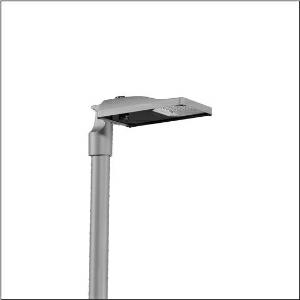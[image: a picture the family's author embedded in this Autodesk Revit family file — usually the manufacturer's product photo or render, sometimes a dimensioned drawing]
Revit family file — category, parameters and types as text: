
# Revit family: streetlight_sl_31_micro___pl52_5xh5h31t08ca_bf49
name_source: partatom
category: Lighting Fixtures
units: mm (PartAtom-declared; Revit-internal decimal feet)

## family parameters
Cut with Voids When Loaded = No
Host = Face
Light Source = No
Part Type = Normal
Room Calculation Point = No
Round Connector Dimension = Use Diameter
Shared = No

## types (1)
- --- (1 x LED, 1420 lm, 10.2 W, 3000K)
    Apparent Load = 10 VA
    CIE Flux Codes = 27 59 98 100 100
    Color Rendering = 70
    Color Temperature = 3000K
    Default Elevation = 1800 mm
    Description = Streetlight SL 31 micro D4i, Desk-Remote mast luminaire for post-top, side-entry; light control with lens of PMMA; light distribution: PL52, direct asymmetric distribution, for standard-compliant lighting for roads and squares; LED: luminous flux: 1.420lm, light colour: 730, colour temperature: 3000K; luminous efficacy: 139,2lm/W; control: pre-setting: logarithmic dimming characteristic, flexible luminous flux parameterisation, time-dependent luminous flux control, constant luminous flux control, power reduction, intelligent temperature release in ECG and LED module, overheat protection; luminaire housing, of diecast aluminium, SITECO metallic grey (DB 702S), corrosivity category C5 high according to DIN EN ISO 12944; cover of toughened safety glass, transparent, opened without tools; mast flange of diecast aluminium, SITECO metallic grey (DB 702S), spigot size: 76/60mm, mast flange included unmounted; with cable H07RN-F 2x 1.5mm², cable length: 5,5m, connection cable pre-assembled; mains connection: 220..240V, AC, 50/60Hz; power consumption (at start of service life): 10,2W / (at end of service life): 10,5W / (with reduced operation 50%): 5,3W; protection rating (complete): IP66; insulation class (complete): insulation class II (safety insulation); impact resistance: IK09; certification: CE, ENEC, ENEC+, VDE, UKCA, ZD4i; permissible operating ambient temperature for outdoor applications: -40..+50°C; packaging unit: 1 piece

Light Distribution: PL52
    Height = 76 mm
    Lamp = 1 x LED
    Lamp Light Flux = 1420 lm
    Lamp Power = 10.2 W
    Lamp count = 1
    Length = 467 mm
    Luminous efficacy = 139 lm/W
    Manufacturer = Siteco
    ModVariant = No
    Model = 5XH5H31T08CA
    Number of Poles = 1
    OnlyDefault = Yes
    Power Factor = 1
    Product Name = Streetlight SL 31 micro | PL52
    Product group = mast luminaire | pylon top
    ProductGroupID = 6100
    Protection Class = Protection class II
    Protection Degree = IP 66
    RLX_Detail_Level = 1
    RLX_Emergency_Light_Flux = 0 lm
    RLX_Emergency_Type = 0
    RLX_Emergency_Type_DB = No
    RlxData = <blob elided: 53873 chars, md5=5cae5641>
    Socket = socket
    Standby Power = 0 W
    System Light Flux = 1420 lm
    System Power = 10 W
    Type Comments = factory setting: luminous flux: 100 % | dim-lin: 254 | 386 mA
    Type Image = l_1300315.jpg
    URL = http://relux.com
    VarID = @adj_055541
    Voltage = 0 V
    Weight = 0.00 kg
    Width = 265 mm

## geometry (parser evidence)
native form markers: Blend x4, Sweep x12
no freeform markers — native parametric forms only
